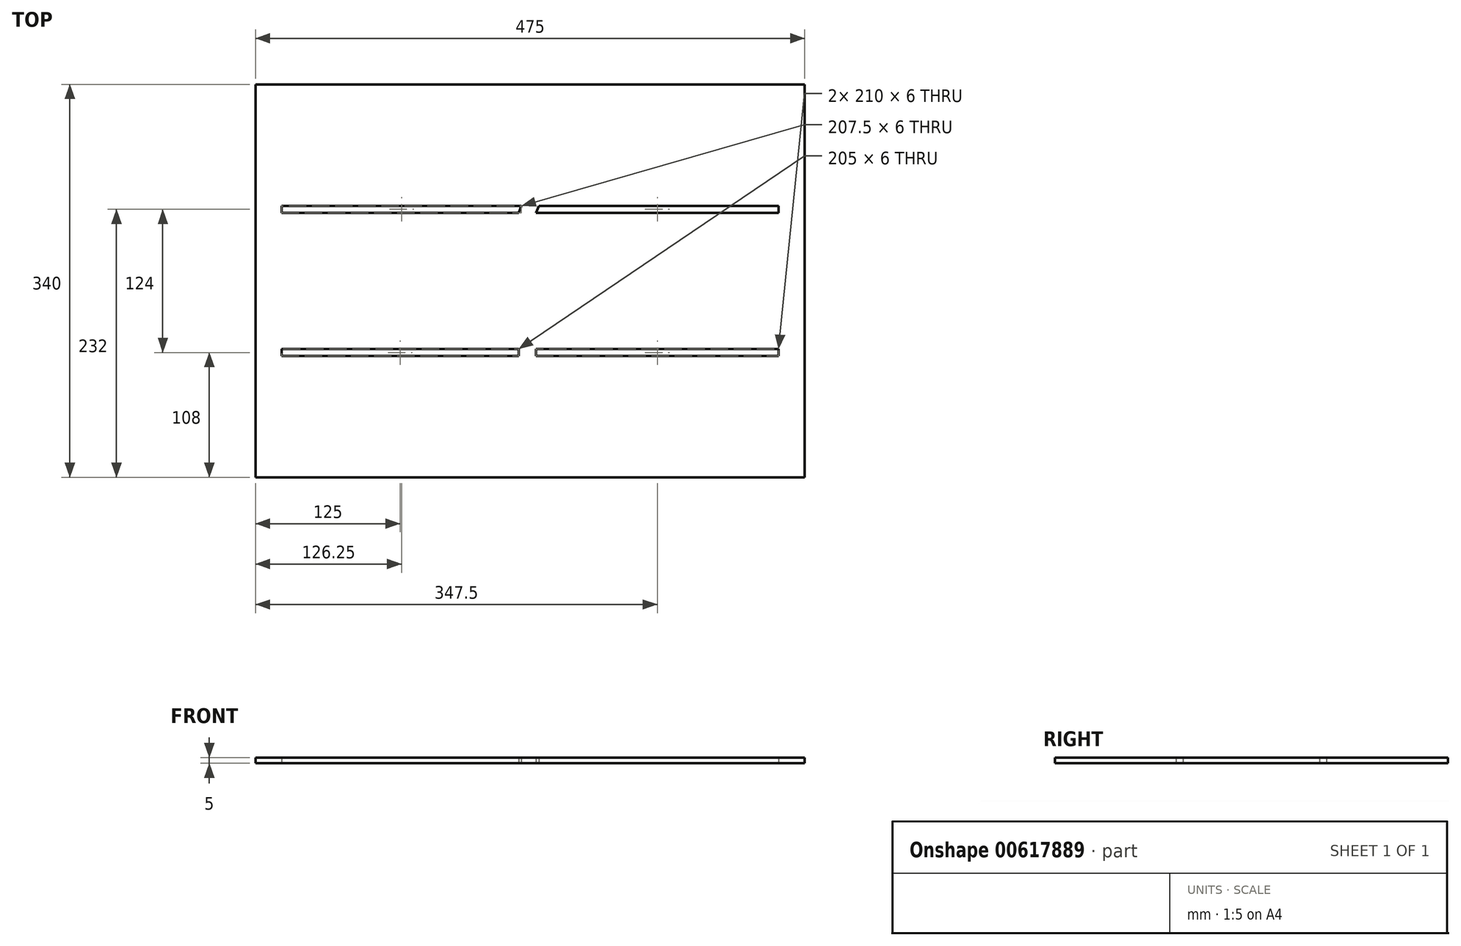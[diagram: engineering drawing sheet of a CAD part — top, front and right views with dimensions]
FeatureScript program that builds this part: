
annotation { "Feature Type Name" : "Feature", "Feature Type Description" : "" }
export const myFeature = defineFeature(function(context is Context, id is Id, definition is map)
    precondition{}
    {
        {
            var Q0;
            Q0=qCreatedBy(makeId("Top.planeOp"),FACE);
            var sketch = newSketch(context, id + "F0", { "sketchPlane" : qUnion([Q0])});
            skLineSegment(sketch, "E0.bottom", {"start": v(-237.5, 170) * mm, "end": v(237.5, 170) * mm});
            skLineSegment(sketch, "E0.top", {"start": v(-237.5, -170) * mm, "end": v(237.5, -170) * mm});
            skLineSegment(sketch, "E0.left", {"start": v(-237.5, 170) * mm, "end": v(-237.5, -170) * mm});
            skLineSegment(sketch, "E0.right", {"start": v(237.5, 170) * mm, "end": v(237.5, -170) * mm});
            skPoint(sketch, "E0.middle", {"position": v(0, 0) * mm});
            skLineSegment(sketch, "E1.bottom", {"start": v(-215, -65) * mm, "end": v(-10, -65) * mm});
            skLineSegment(sketch, "E1.top", {"start": v(-215, -59) * mm, "end": v(-10, -59) * mm});
            skLineSegment(sketch, "E1.left", {"start": v(-215, -59) * mm, "end": v(-215, -65) * mm});
            skLineSegment(sketch, "E1.right", {"start": v(215, -59) * mm, "end": v(215, -65) * mm});
            skPoint(sketch, "E2", {"position": v(0, -65) * mm});
            skLineSegment(sketch, "E3", {"start": v(0, 0) * mm, "end": v(118.05, 0) * mm, "construction": true});
            skLineSegment(sketch, "E4.MirrorCS", {"start": v(-215, 59) * mm, "end": v(-10, 59) * mm});
            skLineSegment(sketch, "E5.MirrorCS", {"start": v(215, 59) * mm, "end": v(215, 65) * mm});
            skLineSegment(sketch, "E6.MirrorCS", {"start": v(-215, 65) * mm, "end": v(-7.5, 65) * mm});
            skLineSegment(sketch, "E7.MirrorCS", {"start": v(-215, 59) * mm, "end": v(-215, 65) * mm});
            skPoint(sketch, "E8", {"position": v(0, 170) * mm});
            skLineSegment(sketch, "E9.left", {"start": v(-10, -59) * mm, "end": v(-10, -65) * mm});
            skLineSegment(sketch, "E9.right", {"start": v(5, -59) * mm, "end": v(5, -65) * mm});
            skLineSegment(sketch, "E10.left", {"start": v(-7.5, 65) * mm, "end": v(-10, 59) * mm});
            skLineSegment(sketch, "E10.right", {"start": v(7.5, 65) * mm, "end": v(5, 59) * mm});
            skLineSegment(sketch, "E11.trimOffspring", {"start": v(7.5, 65) * mm, "end": v(215, 65) * mm});
            skLineSegment(sketch, "E12.trimOffspring", {"start": v(5, 59) * mm, "end": v(215, 59) * mm});
            skLineSegment(sketch, "E13.trimOffspring", {"start": v(5, -59) * mm, "end": v(215, -59) * mm});
            skLineSegment(sketch, "E14.trimOffspring", {"start": v(5, -65) * mm, "end": v(215, -65) * mm});
            skSolve(sketch);
        }
        {
            var Q0;
            Q0=makeQuery(id+"F0.imprint","IMPRINT",FACE,{"disambiguationData":[TD([[makeQuery(id+"F0.imprint","IMPRINT",EDGE,{"derivedFrom":sQuery(id+"F0.wireOp",EDGE,"E0.bottom")}),-1.0]])]});
            extrude(context, id + "F1", {"entities" : qUnion([Q0]), "depth" : 5 * mm, "offsetDistance" : 25 * mm});
        }
    });
